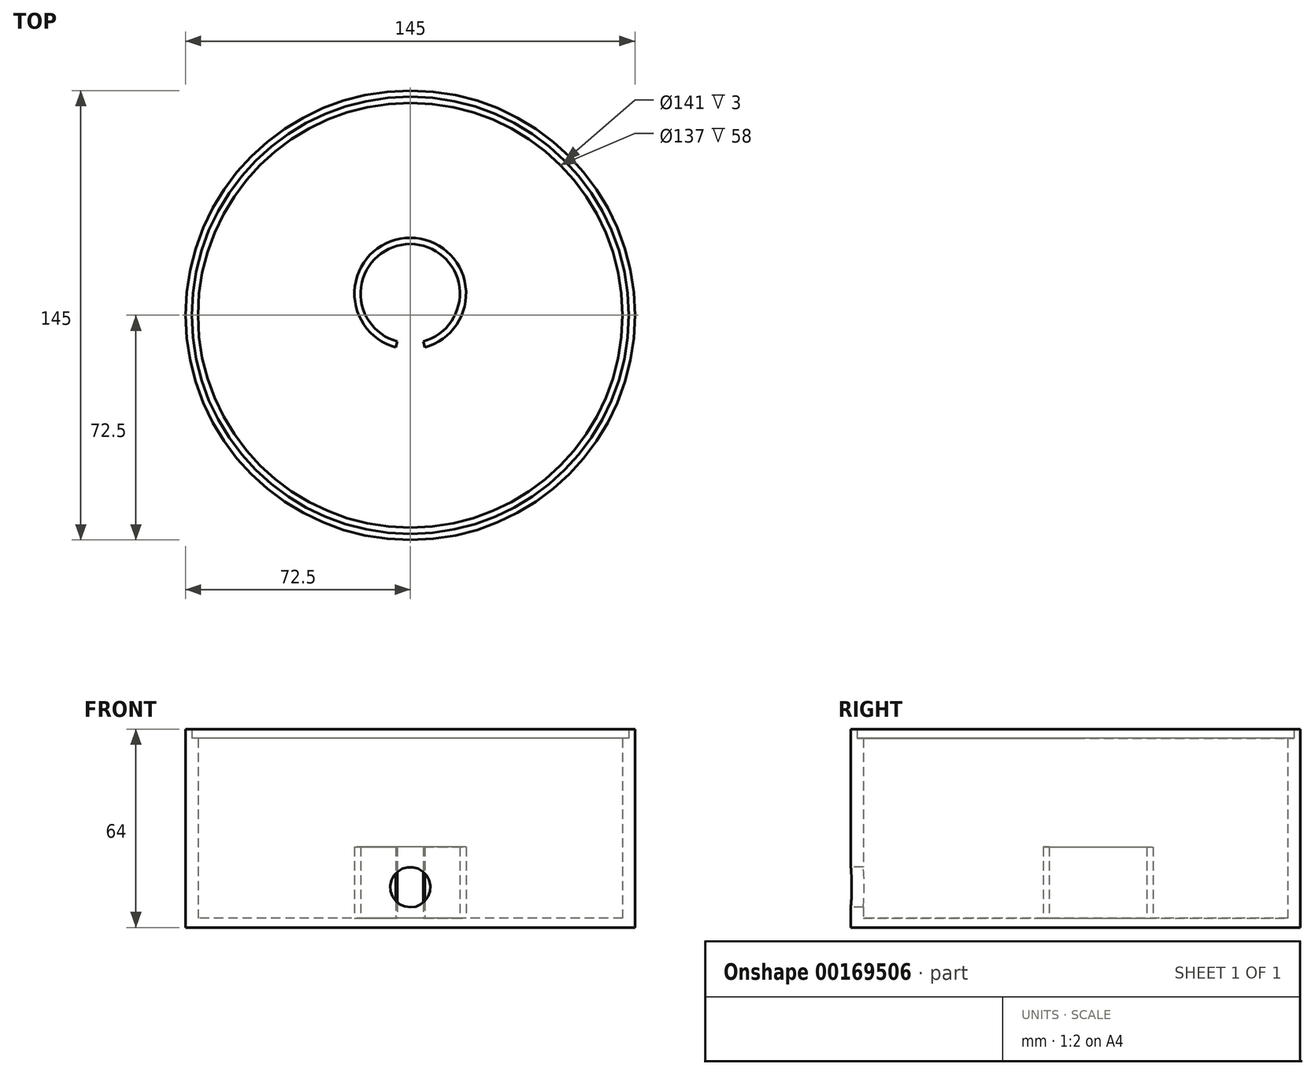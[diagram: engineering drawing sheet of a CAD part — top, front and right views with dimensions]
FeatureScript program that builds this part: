
annotation { "Feature Type Name" : "Feature", "Feature Type Description" : "" }
export const myFeature = defineFeature(function(context is Context, id is Id, definition is map)
    precondition{}
    {
        {
            var Q0;
            Q0=qCreatedBy(makeId("Top.planeOp"),FACE);
            var sketch = newSketch(context, id + "F0", { "sketchPlane" : qUnion([Q0])});
            skCircle(sketch, "E0", {"center": v(0, 0) * mm, "radius": 70.5 * mm});
            skCircle(sketch, "E1", {"center": v(0, 0) * mm, "radius": 72.5 * mm});
            skCircle(sketch, "E2", {"center": v(0, 0) * mm, "radius": 68.5 * mm});
            skSolve(sketch);
        }
        {
            var Q0;
            Q0=makeQuery(id+"F0.imprint","IMPRINT",FACE,{"disambiguationData":[TD([[makeQuery(id+"F0.imprint","IMPRINT",EDGE,{"derivedFrom":sQuery(id+"F0.wireOp",EDGE,"E0")}),-1.0]])]});
            extrude(context, id + "F1", {"entities" : qUnion([Q0]), "depth" : 64 * mm});
        }
        {
            var Q0;
            Q0=makeQuery(id+"F0.imprint","IMPRINT",FACE,{"disambiguationData":[TD([[makeQuery(id+"F0.imprint","IMPRINT",EDGE,{"derivedFrom":sQuery(id+"F0.wireOp",EDGE,"E0")}),1.0]])]});
            extrude(context, id + "F2", {"entities" : qUnion([Q0]), "operationType" : NewBodyOperationType.ADD, "depth" : 61 * mm});
        }
        {
            var Q0;
            Q0=makeQuery(id+"F0.imprint","IMPRINT",FACE,{"disambiguationData":[TD([[makeQuery(id+"F0.imprint","IMPRINT",EDGE,{"derivedFrom":sQuery(id+"F0.wireOp",EDGE,"E2")}),1.0]])]});
            extrude(context, id + "F3", {"entities" : qUnion([Q0]), "operationType" : NewBodyOperationType.ADD, "depth" : 3 * mm});
        }
        {
            var Q0;
            Q0=makeQuery(id+"F3.opExtrude","CAP_FACE",FACE,{"disambiguationData":[OSD([sQuery(id+"F0.wireOp",EDGE,"E2")])],"isStart":false});
            var sketch = newSketch(context, id + "F4", { "sketchPlane" : qUnion([Q0])});
            skCircle(sketch, "E3", {"center": v(0, 7) * mm, "radius": 16 * mm});
            skCircle(sketch, "E4", {"center": v(0, 7) * mm, "radius": 18 * mm});
            skLineSegment(sketch, "E5", {"start": v(0, 7) * mm, "end": v(-4.66, -10.39) * mm});
            skLineSegment(sketch, "E6", {"start": v(0, 7) * mm, "end": v(4.66, -10.39) * mm});
            skLineSegment(sketch, "E7", {"start": v(0, 7) * mm, "end": v(0, -15.38) * mm, "construction": true});
            skSolve(sketch);
        }
        {
            var Q0;
            {var subQ0=sQuery(id+"F4.wireOp",EDGE,"E5");var subQ1=sQuery(id+"F4.wireOp",EDGE,"E3");var subQ2=makeQuery(id+"F4.imprint","INTERSECT",VERTEX,{"derivedFrom":[subQ1,subQ0]});Q0=makeQuery(id+"F4.imprint","IMPRINT",FACE,{"disambiguationData":[TD([[makeQuery(id+"F4.imprint","IMPRINT",EDGE,{"disambiguationData":[TD([[subQ2,1.0]])],"derivedFrom":subQ1}),-1.0]])]});}
            extrude(context, id + "F5", {"entities" : qUnion([Q0]), "operationType" : NewBodyOperationType.ADD, "depth" : (23) * mm});
        }
        {
            var Q0;
            Q0=qCreatedBy(makeId("Front.planeOp"),FACE);
            cPlane(context, id + "F6", {"entities" : qUnion([Q0]), "cplaneType" : CPlaneType.OFFSET, "offset" : 80 * mm, "width" : 150 * mm, "height" : 150 * mm});
        }
        {
            var Q0;
            Q0=qCreatedBy(id+"F6.planeOp",FACE);
            var sketch = newSketch(context, id + "F7", { "sketchPlane" : qUnion([Q0])});
            skLineSegment(sketch, "E8", {"start": v(0, 0) * mm, "end": v(0, 13) * mm, "construction": true});
            skCircle(sketch, "E9", {"center": v(0, 13) * mm, "radius": 6.5 * mm});
            skSolve(sketch);
        }
        {
            var Q0;
            Q0=makeQuery(id+"F7.imprint","IMPRINT",FACE,{"disambiguationData":[TD([[makeQuery(id+"F7.imprint","IMPRINT",EDGE,{"derivedFrom":sQuery(id+"F7.wireOp",EDGE,"E9")}),1.0]])]});
            extrude(context, id + "F8", {"entities" : qUnion([Q0]), "operationType" : NewBodyOperationType.REMOVE, "oppositeDirection" : true, "depth" : 25 * mm});
        }
    });
